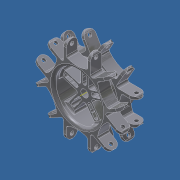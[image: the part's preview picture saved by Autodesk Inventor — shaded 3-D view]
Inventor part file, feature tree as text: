
AUTODESK INVENTOR PART (.ipt)
format: ipt  version: unknown  size: 1,015,296 bytes
history: native  units: in
note: dims shown in document units (in); Inventor stores cm internally (conversion verified against a paired STEP export)
features: extrude x18, sketch x18, pattern_circular x11, fillet x10, other x1, plane x1
ambient origin geometry x8: Origin, YZ Plane, XZ Plane, XY Plane, X Axis, Y Axis, Z Axis, Center Point
bodies: Solid1 (feature_tree)
feature tree (59):
  extrude  "Extrusion1"  Depth=0.75in TaperAngle=0.0deg
  extrude  "Extrusion2"  Depth=0.7156in
  other  "Work Axis1"
  pattern_circular  "Circular Pattern1"  Count=6 Angle=360.0deg
  extrude  "Extrusion3"  Depth=0.1875in
  pattern_circular  "Circular Pattern2"  Count=6 Angle=360.0deg
  fillet  "Fillet1"  Radius=0.125in
  extrude  "Extrusion4"  Depth=0.75in TaperAngle=0.0deg
  extrude  "Extrusion5"  Depth=0.25in TaperAngle=0.0deg
  extrude  "Extrusion6"  Depth=0.75in TaperAngle=0.0deg
  extrude  "Extrusion7"  Depth=0.7156in
  pattern_circular  "Circular Pattern3"  Count=6 Angle=360.0deg
  extrude  "Extrusion8"  Depth=0.1875in
  extrude  "Extrusion9"  Depth=0.75in TaperAngle=0.0deg
  pattern_circular  "Circular Pattern4"  Count=6 Angle=360.0deg
  plane  "Work Plane1"
  fillet  "Fillet2"  [1 undecoded]
  fillet  "Fillet3"  Radius=0.7156in
  fillet  "Fillet4"  Radius=0.7156in
  fillet  "Fillet8"  Radius=0.501in
  fillet  "Fillet9"  Radius=1.0in
  extrude  "Extrusion11"  Depth=0.25in
  pattern_circular  "Circular Pattern6"  [2 undecoded]
  extrude  "Extrusion12"  Depth=1.9685in TaperAngle=360.0deg
  pattern_circular  "Circular Pattern7"  [2 undecoded]
  extrude  "Extrusion10"  Depth=0.125in
  pattern_circular  "Circular Pattern5"  [2 undecoded]
  fillet  "Fillet16"  Radius=0.125in
  extrude  "Extrusion15"  Depth=0.125in
  fillet  "Fillet17"  Radius=0.25in
  pattern_circular  "Circular Pattern9"  [2 undecoded]
  extrude  "Extrusion16"  Depth=0.75in TaperAngle=0.0deg
  extrude  "Extrusion17"  Depth=2.3622in TaperAngle=360.0deg
  pattern_circular  "Circular Pattern10"  [2 undecoded]
  extrude  "Extrusion18"  Depth=0.25in
  extrude  "Extrusion19"  Depth=0.75in TaperAngle=0.0deg
  pattern_circular  "Circular Pattern11"  Count=6 Angle=360.0deg
  fillet  "Fillet18"  Radius=4378.1713in
  fillet  "Fillet21"  Radius=4378.1713in
  extrude  "Extrusion21"  Depth=0.125in
  pattern_circular  "Circular Pattern12"  [2 undecoded]
  sketch  "Sketch1"  dims[d0=6.0in d1=0.75in d2=0.0in]
  sketch  "Sketch2"  dims[d5=1.7in d6=0.7156in]
  sketch  "Sketch3"  dims[d7=0.7156in]
  sketch  "Sketch4"  dims[d8=2.0in]
  sketch  "Sketch5"  dims[d9=2.0in]
  sketch  "Sketch6"  dims[d10=0.75in d11=0.0in d12=2.3622in d13=360.0deg]
  sketch  "Sketch7"  dims[d15=0.1875in d16=0.1875in]
  sketch  "Sketch8"  dims[d17=0.75in d18=0.0in d19=2.3622in d20=360.0deg d22=0.125in]
  sketch  "Sketch9"  dims[d23=3.2in d24=0.75in d25=0.0in]
  sketch  "Sketch10"  dims[d26=3.45in d27=0.25in d28=0.0in]
  sketch  "Sketch11"  dims[d29=6.0in d30=0.75in d31=0.0in]
  sketch  "Sketch12"  dims[d32=0.7156in d33=0.7156in]
  sketch  "Sketch16"  dims[d34=2.0in]
  sketch  "Sketch17"  dims[d35=1.7in]
  sketch  "Sketch18"  dims[d36=0.75in d37=0.0in d38=2.3622in d39=360.0deg]
  sketch  "Sketch19"  dims[d41=0.75in d42=0.0in d43=0.1875in]
  sketch  "Sketch20"  dims[d44=0.1875in d45=0.75in d46=0.0in d47=2.3622in d48=360.0deg d50=-0.875in d51=0.7156in d52=0.7156in d53=0.501in d54=1.0in]
  sketch  "Sketch22"  dims[d55=0.25in d56=0.25in d57=0.75in d58=0.0in d59=1.9685in d60=360.0deg d62=0.125in d63=0.125in d64=0.125in d68=0.125in d69=0.125in d70=0.25in d71=0.25in d72=0.75in d73=0.0in d74=2.3622in d75=360.0deg d77=0.25in d78=0.25in d79=0.75in d80=0.0in d81=2.3622in d82=360.0deg d85=4378.1713in d86=4378.1713in d110=0.125in d111=0.125in d112=0.125in d116=1.0in d117=0.0in d118=0.125in d122=0.95in d123=1.9685in d124=360.0deg d126=0.375in d127=1.0in d128=0.0in d129=0.375in d130=1.0in d131=0.0in d132=2.3622in d133=360.0deg d135=0.375in d136=1.0in d137=0.0in d138=0.375in d139=1.0in d140=0.0in d141=2.3622in d142=360.0deg d146=3.2in d147=1.169in d148=0.465in d149=0.125in d154=0.1875in d155=0.94in d156=0.3in d157=1.0in d158=0.0in d159=1.9685in d160=360.0deg]
note: 13 required parameter values undecoded (feature->parameter linkage not recoverable at this tier; creation-order binding heuristic only, values carry confidence <= 0.55)
